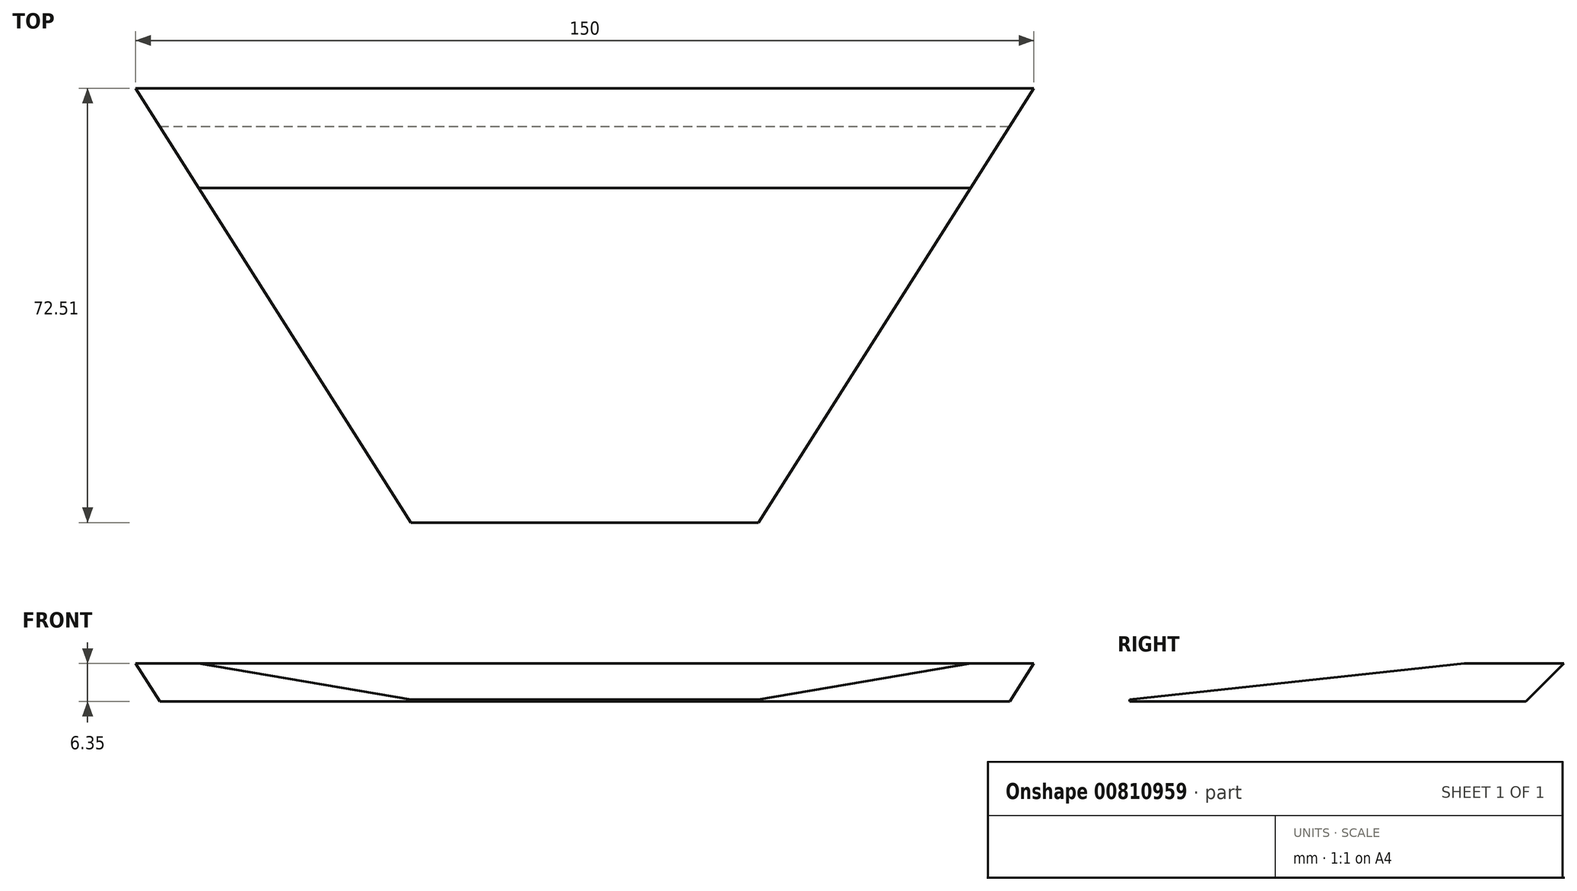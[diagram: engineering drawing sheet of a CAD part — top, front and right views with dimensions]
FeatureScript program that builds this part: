
annotation { "Feature Type Name" : "Feature", "Feature Type Description" : "" }
export const myFeature = defineFeature(function(context is Context, id is Id, definition is map)
    precondition{}
    {
        {
            var Q0;
            Q0=qCreatedBy(makeId("Top.planeOp"),FACE);
            var sketch = newSketch(context, id + "F0", { "sketchPlane" : qUnion([Q0])});
            skPoint(sketch, "E0.middle", {"position": v(0, 0) * mm});
            skLineSegment(sketch, "E1.bottom", {"start": v(-75, 225) * mm, "end": v(75, 225) * mm});
            skLineSegment(sketch, "E2.bottom", {"start": v(-29.02, 152.49) * mm, "end": v(29.02, 152.49) * mm});
            skLineSegment(sketch, "E3", {"start": v(-75, 225) * mm, "end": v(-29.02, 152.49) * mm});
            skLineSegment(sketch, "E4", {"start": v(29.02, 152.49) * mm, "end": v(75, 225) * mm});
            skSolve(sketch);
        }
        {
            var Q0;
            Q0=makeQuery(id+"F0.imprint","IMPRINT",FACE,{"disambiguationData":[TD([[makeQuery(id+"F0.imprint","IMPRINT",EDGE,{"derivedFrom":sQuery(id+"F0.wireOp",EDGE,"E1.bottom")}),-1.0]])]});
            extrude(context, id + "F1", {"entities" : qUnion([Q0]), "depth" : 6.35 * mm, "offsetDistance" : 25.4 * mm});
        }
        {
            var Q0;
            Q0=makeQuery(id+"F1.opExtrude","CAP_EDGE",EDGE,{"disambiguationData":[OSD([sQuery(id+"F0.wireOp",EDGE,"E1.bottom")])],"isStart":true});
            chamfer(context, id + "F2", {"entities" : qUnion([Q0]), "width" : 6.35 * mm, "tangentPropagation" : true});
        }
        {
            var Q0;
            Q0=makeQuery(id+"F1.opExtrude","CAP_EDGE",EDGE,{"disambiguationData":[OSD([sQuery(id+"F0.wireOp",EDGE,"E2.bottom")])],"isStart":false});
            chamfer(context, id + "F3", {"entities" : qUnion([Q0]), "chamferType" : ChamferType.OFFSET_ANGLE, "width" : 55.88 * mm, "oppositeDirection" : false, "angle" : 6.2 * degree, "tangentPropagation" : true});
        }
    });
